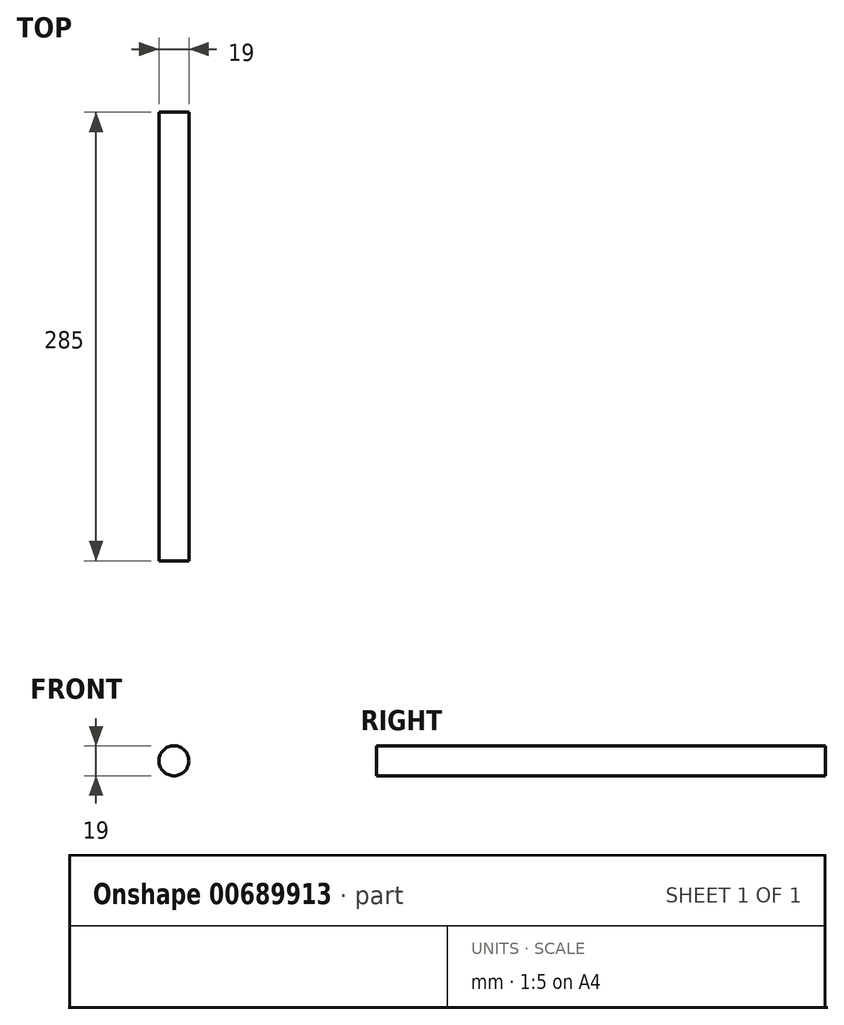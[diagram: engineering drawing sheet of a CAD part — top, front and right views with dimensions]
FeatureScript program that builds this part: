
annotation { "Feature Type Name" : "Feature", "Feature Type Description" : "" }
export const myFeature = defineFeature(function(context is Context, id is Id, definition is map)
    precondition{}
    {
        {
            var Q0;
            Q0=qCreatedBy(makeId("Front.planeOp"),FACE);
            var sketch = newSketch(context, id + "F0", { "sketchPlane" : qUnion([Q0])});
            skCircle(sketch, "E0", {"center": v(0, 0) * mm, "radius": 9.5 * mm});
            skSolve(sketch);
        }
        {
            var Q0;
            Q0 = qSketchRegion(id + "F0", true);
            var Q1;
            Q1=makeQuery(id+"F0.imprint","IMPRINT",FACE,{"disambiguationData":[TD([[makeQuery(id+"F0.imprint","IMPRINT",EDGE,{"derivedFrom":sQuery(id+"F0.wireOp",EDGE,"E0")}),1.0]])]});
            extrude(context, id + "F1", {"entities" : qUnion([Q0, Q1]), "depth" : 285 * mm, "offsetDistance" : 25 * mm});
        }
    });
